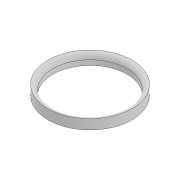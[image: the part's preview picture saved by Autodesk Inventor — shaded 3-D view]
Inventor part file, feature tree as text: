
AUTODESK INVENTOR PART (.ipt)
format: ipt  version: 2021 (Build 250183000, 183)  size: 99,328 bytes
history: native  units: in
note: dims shown in document units (in); Inventor stores cm internally (conversion verified against a paired STEP export)
features: extrude x1, fillet x1, sketch x1
ambient origin geometry x8: Origin, YZ Plane, XZ Plane, XY Plane, X Axis, Y Axis, Z Axis, Center Point
bodies: Solid1 (feature_tree)
feature tree (3):
  extrude  "Extrusion1"  Depth=0.0394in
  fillet  "Fillet1"  Radius=0.0787in
  sketch  "Sketch1"  dims[d0=0.5925in d1=0.0394in d2=0.0787in d3=0.0in d4=0.0394in]
